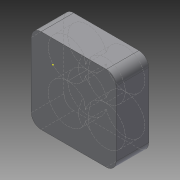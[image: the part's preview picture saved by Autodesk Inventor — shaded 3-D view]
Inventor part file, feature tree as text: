
AUTODESK INVENTOR PART (.ipt)
format: ipt  version: 2015 (Build 190159000, 159)  size: 163,840 bytes
history: native  units: mm
features: fillet x5, hole x4, sketch x3, extrude x1
ambient origin geometry x8: Origin, YZ Plane, XZ Plane, XY Plane, X Axis, Y Axis, Z Axis, Center Point
bodies: Solid1 (feature_tree)
feature tree (13):
  sketch  "Sketch1"  dims[d0=26.0mm d1=26.0mm d2=10.0mm d3=0.0mm d4=3.0mm d5=3.0mm]
  extrude  "Extrusion1"  Depth=26.0mm
  fillet  "Fillet1"  Radius=10.0mm
  fillet  "Fillet2"  Radius=3.0mm
  fillet  "Fillet3"  Radius=3.0mm
  hole  "Hole1"  [1 undecoded]
  hole  "Hole2"  [1 undecoded]
  hole  "Hole3"  [1 undecoded]
  hole  "Hole4"  [1 undecoded]
  fillet  "Fillet4"  [1 undecoded]
  fillet  "Fillet5"  [1 undecoded]
  sketch  "Sketch3"  dims[d7=7.2mm d8=7.0mm d9=12.0mm d10=6.0mm d11=4.0mm d12=2.0mm d13=90.0deg d14=6.0mm d15=20.594885mm d16=7.2mm d17=7.0mm d18=12.0mm d19=6.0mm d20=4.0mm d21=2.0mm d22=90.0deg d23=6.0mm d24=20.594885mm d25=7.0mm d26=7.2mm d27=12.0mm d28=6.0mm d29=4.0mm d30=2.0mm d31=90.0deg d32=6.0mm d33=20.594885mm d34=7.2mm d35=7.0mm d36=12.0mm d37=6.0mm d38=4.0mm d39=2.0mm d40=90.0deg d41=6.0mm d42=20.594885mm d45=3.0mm d46=3.0mm]
  sketch  "Sketch2"  dims[d6=3.0mm]
note: 6 required parameter values undecoded (feature->parameter linkage not recoverable at this tier; creation-order binding heuristic only, values carry confidence <= 0.55)
